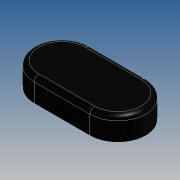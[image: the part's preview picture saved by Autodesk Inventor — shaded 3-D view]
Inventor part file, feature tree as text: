
AUTODESK INVENTOR PART (.ipt)
format: ipt  version: 2015 SP1 (Build 190203100, 203)  size: 211,456 bytes
history: native  units: mm
features: extrude x1, fillet x1, mirror x1, sketch x1
ambient origin geometry x8: Origin, YZ Plane, XZ Plane, XY Plane, X Axis, Y Axis, Z Axis, Center Point
bodies: Solid1 (feature_tree)
feature tree (4):
  extrude  "Extrusion1"  Depth=6.0mm
  fillet  "Fillet1"  Radius=5.0mm
  mirror  "Mirror1"
  sketch  "Sketch1"  dims[d0=12.0mm d1=6.0mm d2=5.0mm d3=0.0mm d4=1.0mm]
